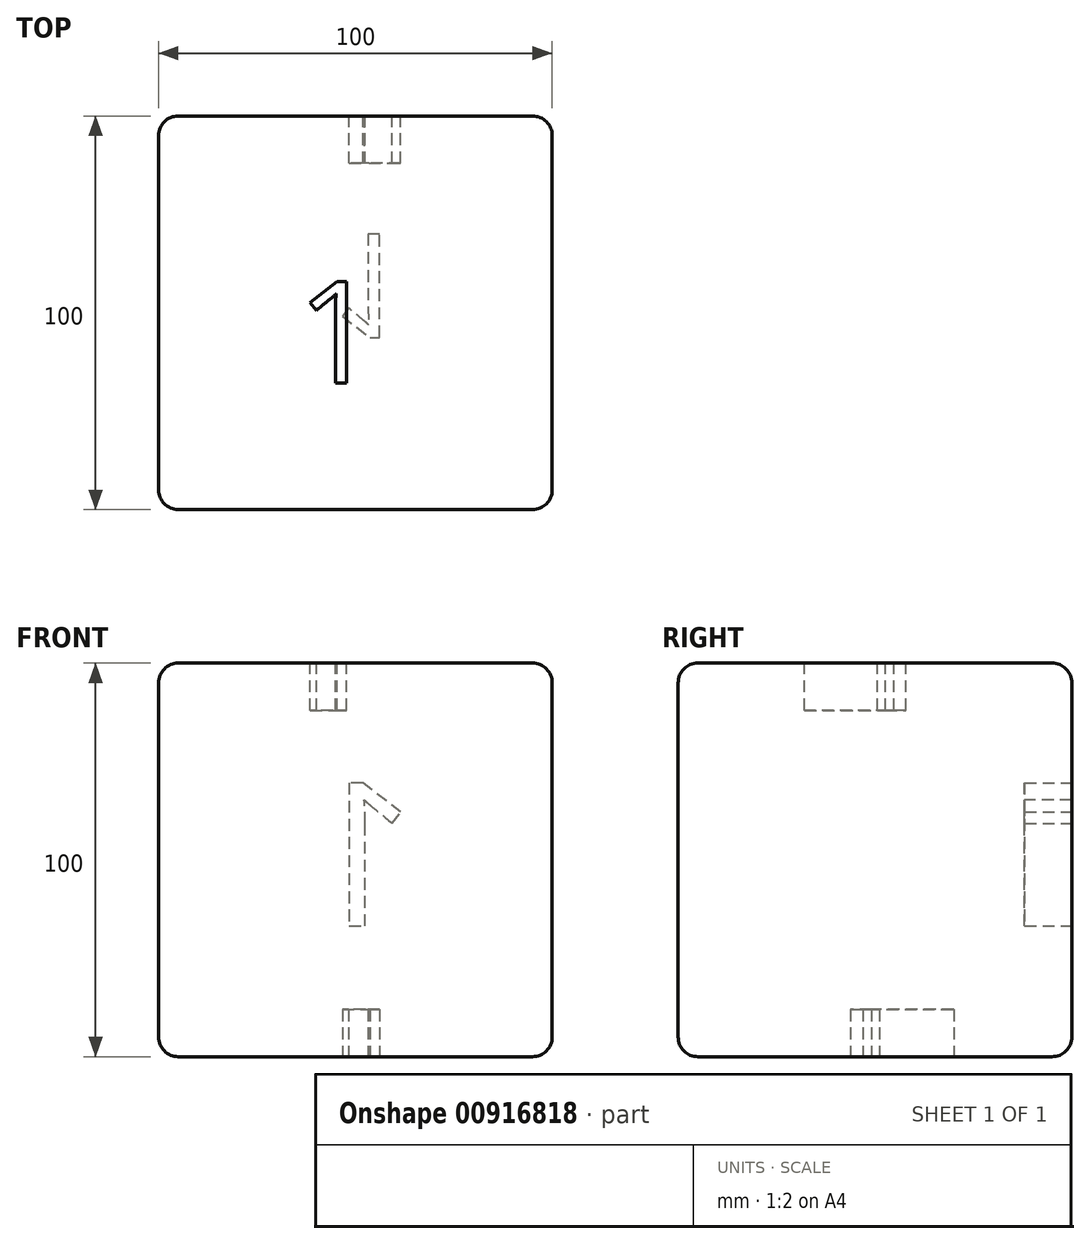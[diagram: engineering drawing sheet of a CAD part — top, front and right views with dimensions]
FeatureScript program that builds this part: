
annotation { "Feature Type Name" : "Feature", "Feature Type Description" : "" }
export const myFeature = defineFeature(function(context is Context, id is Id, definition is map)
    precondition{}
    {
        {
            var Q0;
            Q0=qCreatedBy(makeId("Top.planeOp"),FACE);
            var sketch = newSketch(context, id + "F0", { "sketchPlane" : qUnion([Q0])});
            skLineSegment(sketch, "E0.bottom", {"start": v(-50, 50) * mm, "end": v(50, 50) * mm});
            skLineSegment(sketch, "E0.top", {"start": v(-50, -50) * mm, "end": v(50, -50) * mm});
            skLineSegment(sketch, "E0.left", {"start": v(-50, 50) * mm, "end": v(-50, -50) * mm});
            skLineSegment(sketch, "E0.right", {"start": v(50, 50) * mm, "end": v(50, -50) * mm});
            skPoint(sketch, "E0.middle", {"position": v(0, 0) * mm});
            skSolve(sketch);
        }
        {
            var Q0;
            Q0=makeQuery(id+"F0.imprint","IMPRINT",FACE,{"disambiguationData":[TD([[makeQuery(id+"F0.imprint","IMPRINT",EDGE,{"derivedFrom":sQuery(id+"F0.wireOp",EDGE,"E0.bottom")}),-1.0]])]});
            extrude(context, id + "F1", {"entities" : qUnion([Q0]), "depth" : 100 * mm, "offsetDistance" : 25 * mm});
        }
        {
            var Q0;
            Q0=makeQuery(id+"F1.opExtrude","CAP_EDGE",EDGE,{"disambiguationData":[OSD([sQuery(id+"F0.wireOp",EDGE,"E0.left")])],"isStart":false});
            var Q1;
            Q1=makeQuery(id+"F1.opExtrude","CAP_EDGE",EDGE,{"disambiguationData":[OSD([sQuery(id+"F0.wireOp",EDGE,"E0.bottom")])],"isStart":false});
            var Q2;
            Q2=makeQuery(id+"F1.opExtrude","CAP_EDGE",EDGE,{"disambiguationData":[OSD([sQuery(id+"F0.wireOp",EDGE,"E0.right")])],"isStart":false});
            var Q3;
            Q3=makeQuery(id+"F1.opExtrude","CAP_EDGE",EDGE,{"disambiguationData":[OSD([sQuery(id+"F0.wireOp",EDGE,"E0.top")])],"isStart":false});
            var Q4;
            Q4=makeQuery(id+"F1.opExtrude","SWEPT_EDGE",EDGE,{"disambiguationData":[OSD([sQuery(id+"F0.wireOp",EDGE,"E0.top"),sQuery(id+"F0.wireOp",EDGE,"E0.left")])]});
            var Q5;
            Q5=makeQuery(id+"F1.opExtrude","SWEPT_EDGE",EDGE,{"disambiguationData":[OSD([sQuery(id+"F0.wireOp",EDGE,"E0.bottom"),sQuery(id+"F0.wireOp",EDGE,"E0.left")])]});
            var Q6;
            Q6=makeQuery(id+"F1.opExtrude","CAP_EDGE",EDGE,{"disambiguationData":[OSD([sQuery(id+"F0.wireOp",EDGE,"E0.left")])],"isStart":true});
            var Q7;
            Q7=makeQuery(id+"F1.opExtrude","SWEPT_FACE",FACE,{"disambiguationData":[OSD([sQuery(id+"F0.wireOp",EDGE,"E0.bottom")])]});
            var Q8;
            Q8=makeQuery(id+"F1.opExtrude","SWEPT_EDGE",EDGE,{"disambiguationData":[OSD([sQuery(id+"F0.wireOp",EDGE,"E0.top"),sQuery(id+"F0.wireOp",EDGE,"E0.right")])]});
            var Q9;
            Q9=makeQuery(id+"F1.opExtrude","CAP_EDGE",EDGE,{"disambiguationData":[OSD([sQuery(id+"F0.wireOp",EDGE,"E0.right")])],"isStart":true});
            var Q10;
            Q10=makeQuery(id+"F1.opExtrude","CAP_EDGE",EDGE,{"disambiguationData":[OSD([sQuery(id+"F0.wireOp",EDGE,"E0.top")])],"isStart":true});
            fillet(context, id + "F2", {"entities" : qUnion([Q0, Q1, Q2, Q3, Q4, Q5, Q6, Q7, Q8, Q9, Q10]), "radius" : 5 * mm, "tangentPropagation" : true, "allowEdgeOverflow" : false});
        }
        {
            var Q0;
            Q0=makeQuery(id+"F1.opExtrude","CAP_FACE",FACE,{"disambiguationData":[OSD([sQuery(id+"F0.wireOp",EDGE,"E0.bottom"),sQuery(id+"F0.wireOp",EDGE,"E0.top"),sQuery(id+"F0.wireOp",EDGE,"E0.left"),sQuery(id+"F0.wireOp",EDGE,"E0.right")])],"isStart":false});
            var sketch = newSketch(context, id + "F3", { "sketchPlane" : qUnion([Q0])});
            skText(sketch, "E1", { "text": "1", "fontName": "OpenSans-Regular.ttf"});
            const initialGuessF3  = {"E1": [-0.0148, -0.01786, 1, 0, 0.02598]};
            skSetInitialGuess(sketch, initialGuessF3);
            skSolve(sketch);
        }
        {
            var Q0;
            Q0 = qSketchRegion(id + "F3", true);
            extrude(context, id + "F4", {"entities" : qUnion([Q0]), "operationType" : NewBodyOperationType.REMOVE, "oppositeDirection" : true, "depth" : 12 * mm, "offsetDistance" : 25 * mm});
        }
        {
            var Q0;
            Q0=makeQuery(id+"F1.opExtrude","CAP_FACE",FACE,{"disambiguationData":[OSD([sQuery(id+"F0.wireOp",EDGE,"E0.bottom"),sQuery(id+"F0.wireOp",EDGE,"E0.top"),sQuery(id+"F0.wireOp",EDGE,"E0.left"),sQuery(id+"F0.wireOp",EDGE,"E0.right")])],"isStart":true});
            var sketch = newSketch(context, id + "F5", { "sketchPlane" : qUnion([Q0])});
            skText(sketch, "E2", { "text": "1", "fontName": "OpenSans-Regular.ttf"});
            const initialGuessF5  = {"E2": [-0.00667, -0.02003, 1, 0, 0.02649]};
            skSetInitialGuess(sketch, initialGuessF5);
            skSolve(sketch);
        }
        {
            var Q0;
            Q0 = qSketchRegion(id + "F5", true);
            extrude(context, id + "F6", {"entities" : qUnion([Q0]), "operationType" : NewBodyOperationType.REMOVE, "oppositeDirection" : true, "depth" : 12 * mm, "offsetDistance" : 25 * mm});
        }
        {
            var Q0;
            Q0=makeQuery(id+"F1.opExtrude","SWEPT_FACE",FACE,{"disambiguationData":[OSD([sQuery(id+"F0.wireOp",EDGE,"E0.bottom")])]});
            var sketch = newSketch(context, id + "F7", { "sketchPlane" : qUnion([Q0])});
            skText(sketch, "E3", { "text": "1", "fontName": "OpenSans-Regular.ttf"});
            const initialGuessF7  = {"E3": [-0.01203, 0.04353, 1, 0, 0.01907]};
            skSetInitialGuess(sketch, initialGuessF7);
            skSolve(sketch);
        }
        {
            var Q0;
            Q0 = qSketchRegion(id + "F7", true);
            extrude(context, id + "F8", {"entities" : qUnion([Q0]), "operationType" : NewBodyOperationType.REMOVE, "depth" : 12 * mm, "offsetDistance" : 25 * mm});
        }
        {
            var Q0;
            Q0=makeQuery(id+"F1.opExtrude","SWEPT_FACE",FACE,{"disambiguationData":[OSD([sQuery(id+"F0.wireOp",EDGE,"E0.bottom")])]});
            var sketch = newSketch(context, id + "F9", { "sketchPlane" : qUnion([Q0])});
            skText(sketch, "E4", { "text": "1", "fontName": "OpenSans-Regular.ttf"});
            const initialGuessF9  = {"E4": [-0.0162, 0.03321, 1, 0, 0.03669]};
            skSetInitialGuess(sketch, initialGuessF9);
            skSolve(sketch);
        }
        {
            var Q0;
            Q0 = qSketchRegion(id + "F9", true);
            extrude(context, id + "F10", {"entities" : qUnion([Q0]), "operationType" : NewBodyOperationType.REMOVE, "oppositeDirection" : true, "depth" : 12 * mm, "offsetDistance" : 25 * mm});
        }
    });
